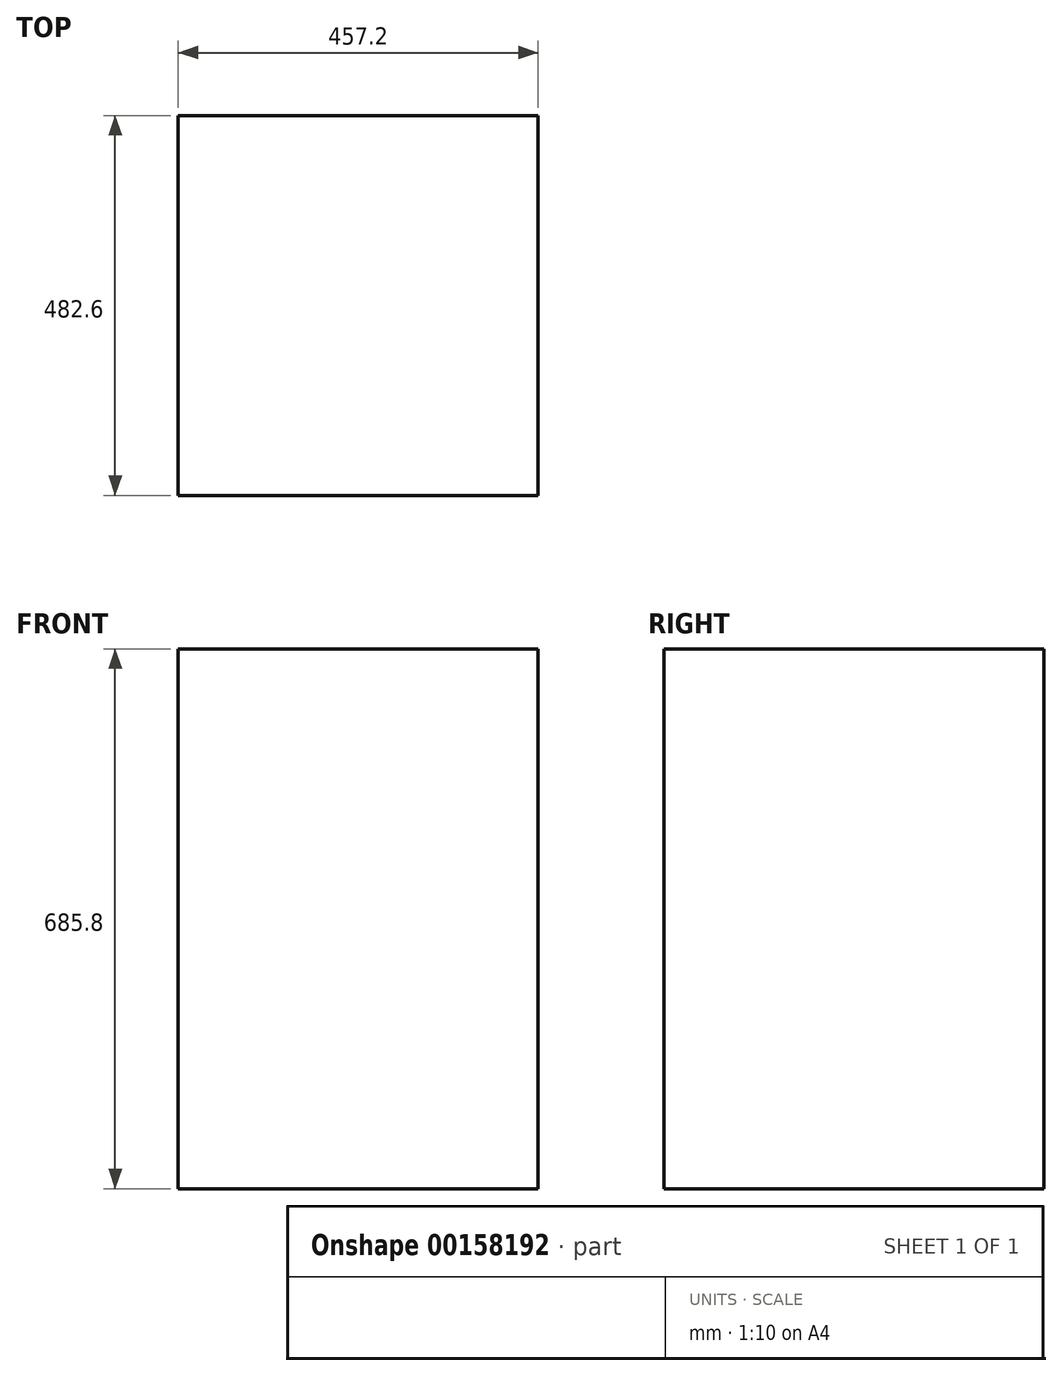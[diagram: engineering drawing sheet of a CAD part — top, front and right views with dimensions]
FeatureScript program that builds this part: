
annotation { "Feature Type Name" : "Feature", "Feature Type Description" : "" }
export const myFeature = defineFeature(function(context is Context, id is Id, definition is map)
    precondition{}
    {
        {
            var Q0;
            Q0=qCreatedBy(makeId("Front.planeOp"),FACE);
            var sketch = newSketch(context, id + "F0", { "sketchPlane" : qUnion([Q0])});
            skLineSegment(sketch, "E0.bottom", {"start": v(0, 0) * mm, "end": v(457.2, 0) * mm});
            skLineSegment(sketch, "E0.top", {"start": v(0, -685.8) * mm, "end": v(457.2, -685.8) * mm});
            skLineSegment(sketch, "E0.left", {"start": v(0, 0) * mm, "end": v(0, -685.8) * mm});
            skLineSegment(sketch, "E0.right", {"start": v(457.2, 0) * mm, "end": v(457.2, -685.8) * mm});
            skSolve(sketch);
        }
        {
            var Q0;
            Q0=makeQuery(id+"F0.imprint","IMPRINT",FACE,{"disambiguationData":[TD([[makeQuery(id+"F0.imprint","IMPRINT",EDGE,{"derivedFrom":sQuery(id+"F0.wireOp",EDGE,"E0.bottom")}),-1.0]])]});
            extrude(context, id + "F1", {"entities" : qUnion([Q0]), "depth" : 482.6 * mm});
        }
    });
